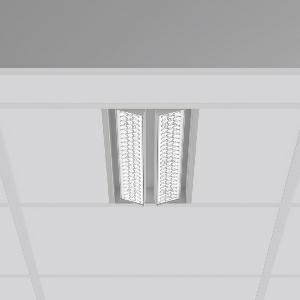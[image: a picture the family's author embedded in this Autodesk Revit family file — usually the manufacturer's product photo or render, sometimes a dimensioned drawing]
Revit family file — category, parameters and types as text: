
# Revit family: tx-move_901736_004_1_76_90ae
name_source: partatom
category: Lighting Fixtures
units: mm (PartAtom-declared; Revit-internal decimal feet)

## family parameters
Cut with Voids When Loaded = No
Host = Face
Light Source = No
Part Type = Normal
Room Calculation Point = No
Round Connector Dimension = Use Diameter
Shared = No

## types (1)
- MultiLumen 1 (1 x LED Modul 840, 2800 lm, 4000)
    Apparent Load = 35 VA
    Approval mark = CE
    CIE Flux Codes = 90 97 99 100 100
    Color Rendering = 80
    Color Temperature = 4000
    Default Elevation = 1800 mm
    Description = Series: TX-MOVE
Einlege/Einbau-Flächenstrahler. Housing: sheet steel, powder-coated. 2xSwivel range: 90°. High-efficiency LED units with optimum light control thanks to clear plastic (PC) lens optics. Spezielle Mikrostrukturen reduzieren Gelbsaum. Symmetrical light distribution. Suitable for laying in grid ceiling module 625. Connected converter included in separate gearbox.Suitable for through-wiring.MultiLumen: Luminous flux adjustable in 3 steps. Accessories: Mounting frame for installation in suspended ceilings. Environmentally friendly and resource-saving due to replaceable and recyclable components. 
Colour: silver, matt (approx. RAL 9006)
Length: 622 mm
Width: 190 mm
Height: 39 mm
Cut-out length: 602 mm
Cut-out width: 174 mm
Recess height: 100 mm
Lamp: LED
Socket: without socket
Colour temperature: 4000K
Colour rendering index (CRI): 80
System power: 35 W
Rated luminous flux: 5600 lm
Luminous efficiency: 160 lm/W
System power 2: 47 W
Rated luminous flux 2: 7300 lm
Luminous efficiency 2: 155 lm/W
System power 3: 68 W
Rated luminous flux 3: 10000 lm
Luminous efficiency 3: 147 lm/W
Control gear: Dimmable EVG, DALI
Protection class: I
Type of protection: IP 20
    Height = 0 mm  [stored 0 ft]
    Lamp = 1 x LED Modul 840
    Lamp Light Flux = 2800 lm
    Lamp count = 1
    Length = 622 mm
    Lifetime = 50000 h
    Luminous efficacy = 160 lm/W
    Manufacturer = RZB
    ModVariant = No
    Model = 901736.004.1.76
    Mounting Place = Ceiling, Wall
    Mounting Type = Recessed
    Number of Poles = 1
    OnlyDefault = Yes
    Power Factor = 1
    Product Name = TX-MOVE
    Product group = Recessed projectors
    ProductGroupID = 401
    Protection Class = Protection class I
    Protection Degree = IP 20
    RLX_Detail_Level = 1
    RLX_Emergency_Light_Flux = 0 lm
    RLX_Emergency_Type = 0
    RLX_Emergency_Type_DB = No
    RlxData = <blob elided: 34381 chars, md5=681abcac>
    Socket = socket
    Standby Power = 0 W
    System Light Flux = 5600 lm
    System Power = 35 W
    Type Comments = MultiLumen 1
    Type Image = 901737.004.jpg
    URL = http://relux.com
    VarID = multilumen_1
    Voltage = 230 V
    Voltage Range = 220-240 V
    Weight = 0.00 kg
    Width = 190 mm  [stored 0.62336 ft]

note: [stored X ft] marks values corroborated as IEEE doubles in the binary element streams (Revit-internal decimal feet)

## geometry (parser evidence)
native form markers: Blend x4, Sweep x16
no freeform markers — native parametric forms only
